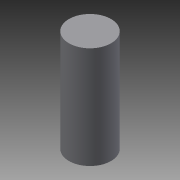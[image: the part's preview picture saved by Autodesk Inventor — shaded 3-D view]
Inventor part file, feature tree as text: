
AUTODESK INVENTOR PART (.ipt)
format: ipt  version: 2015 SP1 (Build 190203100, 203)  size: 82,432 bytes
history: native  units: mm
features: extrude x1, sketch x1
ambient origin geometry x8: Origin, YZ Plane, XZ Plane, XY Plane, X Axis, Y Axis, Z Axis, Center Point
bodies: Solid1 (feature_tree)
feature tree (2):
  extrude  "Extrusion1"  TaperAngle=0.0deg  [1 undecoded]
  sketch  "Sketch1"  dims[d2=0.0mm d3=0.0mm d4=0.0mm d9=0.0mm d10=0.0mm]
note: 1 required parameter value undecoded (feature->parameter linkage not recoverable at this tier; creation-order binding heuristic only, values carry confidence <= 0.55)
